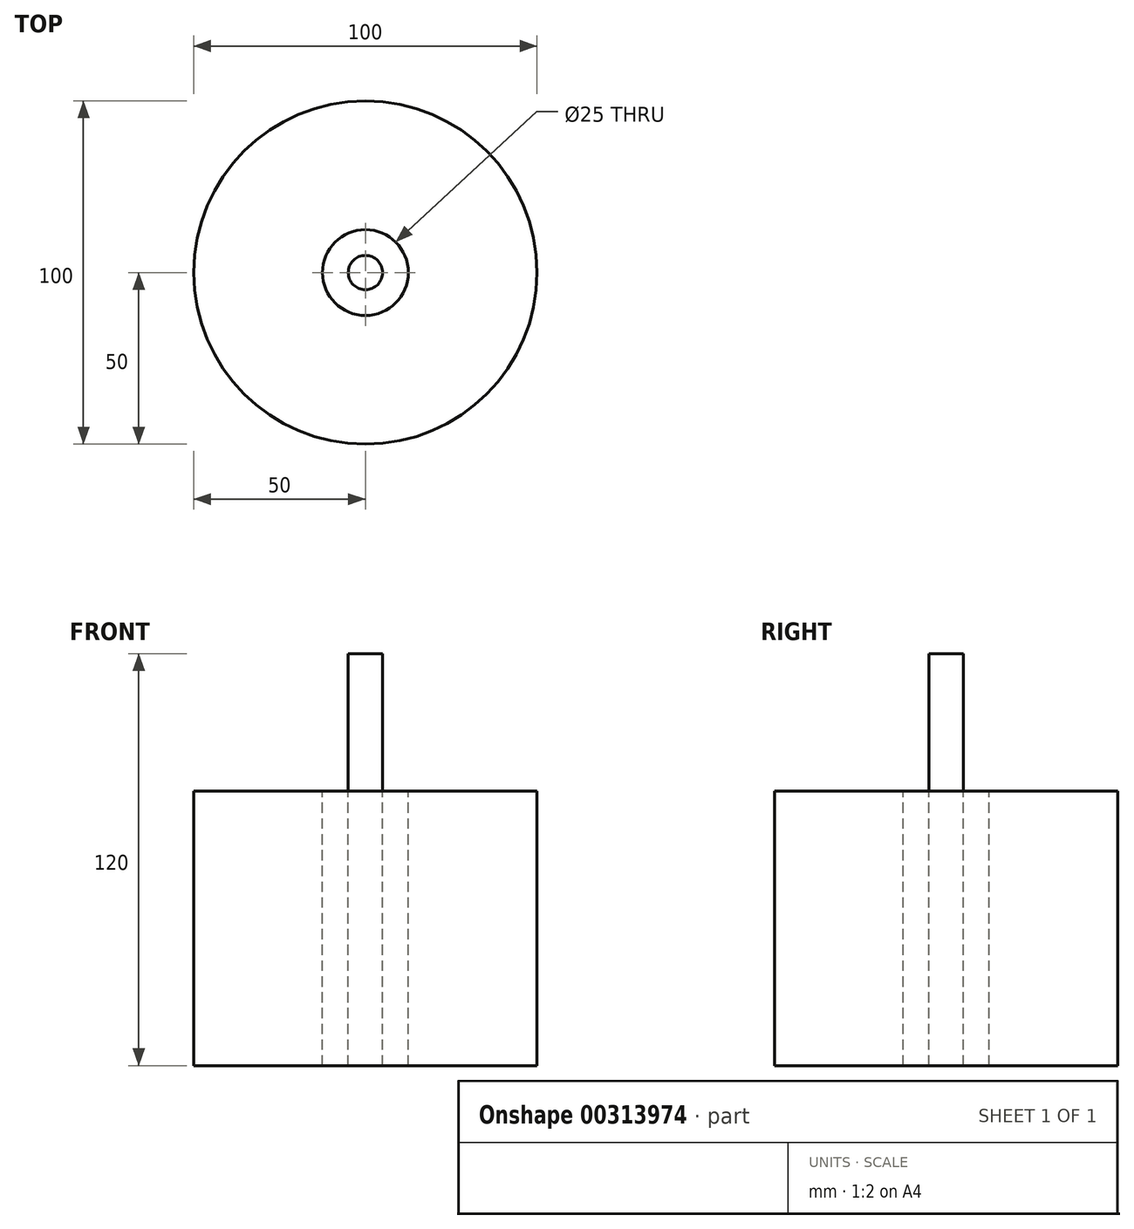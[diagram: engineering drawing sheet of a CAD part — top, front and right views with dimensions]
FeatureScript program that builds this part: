
annotation { "Feature Type Name" : "Feature", "Feature Type Description" : "" }
export const myFeature = defineFeature(function(context is Context, id is Id, definition is map)
    precondition{}
    {
        {
            var Q0;
            Q0=qCreatedBy(makeId("Top.planeOp"),FACE);
            var sketch = newSketch(context, id + "F0", { "sketchPlane" : qUnion([Q0])});
            skCircle(sketch, "E0", {"center": v(0, 0) * mm, "radius": 50 * mm});
            skCircle(sketch, "E1", {"center": v(0, 0) * mm, "radius": 42.5 * mm});
            skCircle(sketch, "E2", {"center": v(0, 0) * mm, "radius": 12.5 * mm});
            skCircle(sketch, "E3", {"center": v(0, 0) * mm, "radius": 5 * mm});
            skSolve(sketch);
        }
        {
            var Q0;
            Q0=makeQuery(id+"F0.imprint","IMPRINT",FACE,{"disambiguationData":[TD([[makeQuery(id+"F0.imprint","IMPRINT",EDGE,{"derivedFrom":sQuery(id+"F0.wireOp",EDGE,"E0")}),1.0]])]});
            var Q1;
            Q1=makeQuery(id+"F0.imprint","IMPRINT",FACE,{"disambiguationData":[TD([[makeQuery(id+"F0.imprint","IMPRINT",EDGE,{"derivedFrom":sQuery(id+"F0.wireOp",EDGE,"E1")}),1.0]])]});
            var Q2;
            Q2=makeQuery(id+"F0.imprint","IMPRINT",FACE,{"disambiguationData":[TD([[makeQuery(id+"F0.imprint","IMPRINT",EDGE,{"derivedFrom":sQuery(id+"F0.wireOp",EDGE,"E3")}),1.0]])]});
            extrude(context, id + "F1", {"entities" : qUnion([Q0, Q1, Q2]), "oppositeDirection" : true, "depth" : 30 * mm});
        }
        {
            var Q0;
            Q0=makeQuery(id+"F1.opExtrude","CAP_FACE",FACE,{"disambiguationData":[OSD([sQuery(id+"F0.wireOp",EDGE,"E3")])],"isStart":true});
            extrude(context, id + "F2", {"entities" : qUnion([Q0]), "operationType" : NewBodyOperationType.ADD, "depth" : 90 * mm});
        }
        {
            var Q0;
            Q0=makeQuery(id+"F1.opExtrude","CAP_FACE",FACE,{"disambiguationData":[OSD([sQuery(id+"F0.wireOp",EDGE,"E0"),sQuery(id+"F0.wireOp",EDGE,"E2")])],"isStart":true});
            var Q1;
            Q1=makeQuery(id+"F1.opExtrude","CAP_FACE",FACE,{"disambiguationData":[OSD([sQuery(id+"F0.wireOp",EDGE,"E0"),sQuery(id+"F0.wireOp",EDGE,"E2")])],"isStart":false});
            extrude(context, id + "F3", {"entities" : qUnion([Q0, Q1]), "operationType" : NewBodyOperationType.ADD, "depth" : 50 * mm});
        }
    });
